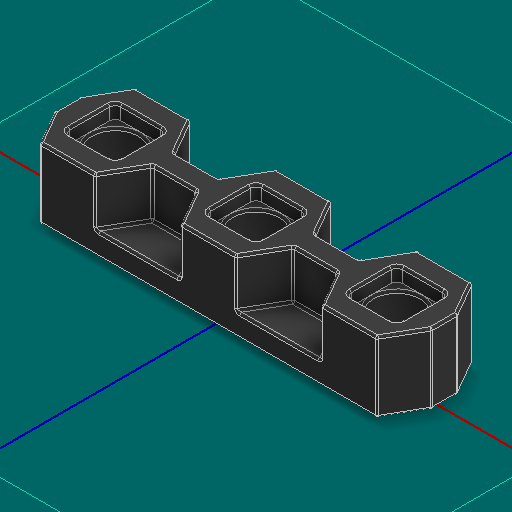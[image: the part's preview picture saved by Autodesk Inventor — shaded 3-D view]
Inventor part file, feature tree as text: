
AUTODESK INVENTOR PART (.ipt)
format: ipt  version: 2025 (Build 290162000, 162)  size: 505,856 bytes
history: native  units: in
note: dims shown in document units (in); Inventor stores cm internally (conversion verified against a paired STEP export)
features: other x3, sketch x1
ambient origin geometry x8: Origin, YZ Plane, XZ Plane, XY Plane, X Axis, Y Axis, Z Axis, Center Point
bodies: Solid1 (feature_tree)
feature tree (4):
  other  "Bearing Flat Low Profile.ipt"
  other  "Solid1::Bearing Flat Low Profile.ipt"
  other  "TaggingFeature1"
  sketch  "Sketch1"  dims[d0=0.3937in]
